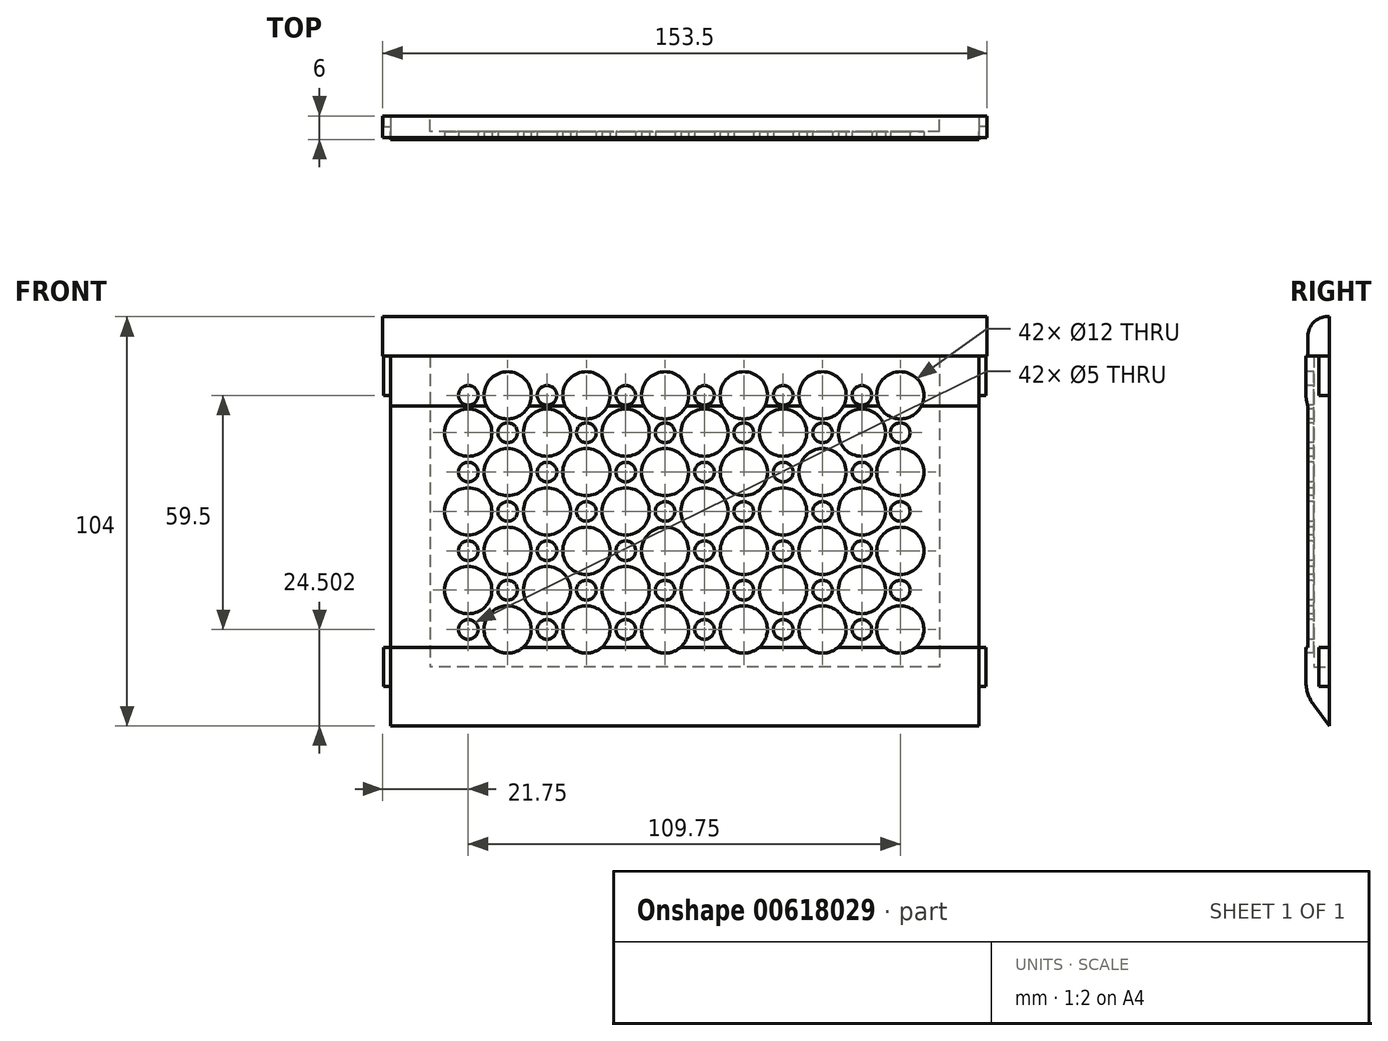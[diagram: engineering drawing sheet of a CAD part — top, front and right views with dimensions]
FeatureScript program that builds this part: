
annotation { "Feature Type Name" : "Feature", "Feature Type Description" : "" }
export const myFeature = defineFeature(function(context is Context, id is Id, definition is map)
    precondition{}
    {
        {
            var Q0;
            Q0=qCreatedBy(makeId("Right.planeOp"),FACE);
            var sketch = newSketch(context, id + "F0", { "sketchPlane" : qUnion([Q0])});
            skLineSegment(sketch, "E0", {"start": v(5.5, 58.2) * mm, "end": v(5.5, -45.8) * mm});
            skLineSegment(sketch, "E1", {"start": v(5.5, 38.2) * mm, "end": v(2.5, 38.2) * mm});
            skLineSegment(sketch, "E2", {"start": v(2.5, 38.2) * mm, "end": v(2.5, 48.2) * mm});
            skLineSegment(sketch, "E3", {"start": v(2.5, 48.2) * mm, "end": v(-0.5, 48.2) * mm});
            skLineSegment(sketch, "E4", {"start": v(-0.5, 48.2) * mm, "end": v(-0.5, 36.2) * mm});
            skLineSegment(sketch, "E5", {"start": v(-0.5, 36.2) * mm, "end": v(5.5, 28.2) * mm});
            skLineSegment(sketch, "E6", {"start": v(5.5, -45.8) * mm, "end": v(-0.5, -37.8) * mm});
            skLineSegment(sketch, "E7", {"start": v(-0.5, -37.8) * mm, "end": v(-0.5, -25.8) * mm});
            skLineSegment(sketch, "E8", {"start": v(-0.5, -25.8) * mm, "end": v(2.5, -25.8) * mm});
            skLineSegment(sketch, "E9", {"start": v(2.5, -25.8) * mm, "end": v(2.5, -35.8) * mm});
            skLineSegment(sketch, "E10", {"start": v(2.5, -35.8) * mm, "end": v(5.5, -35.8) * mm});
            skLineSegment(sketch, "E11.bottom", {"start": v(5.5, 58.2) * mm, "end": v(0, 58.2) * mm});
            skLineSegment(sketch, "E11.top", {"start": v(5.5, -45.8) * mm, "end": v(0, -45.8) * mm});
            skLineSegment(sketch, "E11.right", {"start": v(0, 58.2) * mm, "end": v(0, -45.8) * mm});
            skSolve(sketch);
        }
        {
            var Q0;
            {var subQ5=sQuery(id+"F0.wireOp",EDGE,"E1");Q0=makeQuery(id+"F0.imprint","IMPRINT",FACE,{"disambiguationData":[TD([[makeQuery(id+"F0.imprint","IMPRINT",EDGE,{"derivedFrom":subQ5}),-1.0]])]});}
            var Q1;
            {var subQ8=sQuery(id+"F0.wireOp",EDGE,"E1");Q1=makeQuery(id+"F0.imprint","IMPRINT",FACE,{"disambiguationData":[TD([[makeQuery(id+"F0.imprint","IMPRINT",EDGE,{"derivedFrom":subQ8}),1.0]])]});}
            var Q2;
            {var subQ1=sQuery(id+"F0.wireOp",EDGE,"E9");Q2=makeQuery(id+"F0.imprint","IMPRINT",FACE,{"disambiguationData":[TD([[makeQuery(id+"F0.imprint","IMPRINT",EDGE,{"derivedFrom":subQ1}),1.0]])]});}
            var Q3;
            {var subQ1=sQuery(id+"F0.wireOp",EDGE,"E9");Q3=makeQuery(id+"F0.imprint","IMPRINT",FACE,{"disambiguationData":[TD([[makeQuery(id+"F0.imprint","IMPRINT",EDGE,{"derivedFrom":subQ1}),-1.0]])]});}
            var Q4;
            {var subQ0=sQuery(id+"F0.wireOp",EDGE,"E4");Q4=makeQuery(id+"F0.imprint","IMPRINT",FACE,{"disambiguationData":[TD([[makeQuery(id+"F0.imprint","IMPRINT",EDGE,{"derivedFrom":subQ0}),1.0]])]});}
            var Q5;
            {var subQ0=sQuery(id+"F0.wireOp",EDGE,"E7");Q5=makeQuery(id+"F0.imprint","IMPRINT",FACE,{"disambiguationData":[TD([[makeQuery(id+"F0.imprint","IMPRINT",EDGE,{"derivedFrom":subQ0}),-1.0]])]});}
            extrude(context, id + "F1", {"entities" : qUnion([Q0, Q1, Q2, Q3, Q4, Q5]), "oppositeDirection" : true, "depth" : 149.5 * mm, "offsetDistance" : 25 * mm});
        }
        {
            var Q0;
            Q0=makeQuery(id+"F1.opExtrude","CAP_FACE",FACE,{"disambiguationData":[OSD([sQuery(id+"F0.wireOp",EDGE,"E3"),sQuery(id+"F0.wireOp",EDGE,"E4"),sQuery(id+"F0.wireOp",EDGE,"E5"),sQuery(id+"F0.wireOp",EDGE,"E6"),sQuery(id+"F0.wireOp",EDGE,"E7"),sQuery(id+"F0.wireOp",EDGE,"E8"),sQuery(id+"F0.wireOp",EDGE,"E11.bottom"),sQuery(id+"F0.wireOp",EDGE,"E0"),sQuery(id+"F0.wireOp",EDGE,"E11.right")])],"isStart":false});
            var sketch = newSketch(context, id + "F2", { "sketchPlane" : qUnion([Q0])});
            skLineSegment(sketch, "E12.bottom", {"start": v(-5.5, 48.2) * mm, "end": v(-2.75, 48.2) * mm});
            skLineSegment(sketch, "E12.top", {"start": v(-5.5, 38.2) * mm, "end": v(-2.75, 38.2) * mm});
            skLineSegment(sketch, "E12.left", {"start": v(-5.5, 48.2) * mm, "end": v(-5.5, 38.2) * mm});
            skLineSegment(sketch, "E12.right", {"start": v(-2.75, 48.2) * mm, "end": v(-2.75, 38.2) * mm});
            skLineSegment(sketch, "E13.bottom", {"start": v(-5.5, -25.8) * mm, "end": v(-2.75, -25.8) * mm});
            skLineSegment(sketch, "E13.top", {"start": v(-5.5, -35.8) * mm, "end": v(-2.75, -35.8) * mm});
            skLineSegment(sketch, "E13.left", {"start": v(-5.5, -25.8) * mm, "end": v(-5.5, -35.8) * mm});
            skLineSegment(sketch, "E13.right", {"start": v(-2.75, -25.8) * mm, "end": v(-2.75, -35.8) * mm});
            skSolve(sketch);
        }
        {
            var Q0;
            Q0=makeQuery(id+"F2.imprint","IMPRINT",FACE,{"disambiguationData":[TD([[makeQuery(id+"F2.imprint","IMPRINT",EDGE,{"derivedFrom":sQuery(id+"F2.wireOp",EDGE,"E12.bottom")}),-1.0]])]});
            var Q1;
            Q1=makeQuery(id+"F2.imprint","IMPRINT",FACE,{"disambiguationData":[TD([[makeQuery(id+"F2.imprint","IMPRINT",EDGE,{"derivedFrom":sQuery(id+"F2.wireOp",EDGE,"E13.bottom")}),-1.0]])]});
            extrude(context, id + "F3", {"entities" : qUnion([Q0, Q1]), "operationType" : NewBodyOperationType.ADD, "depth" : 1.75 * mm, "offsetDistance" : 25 * mm});
        }
        {
            var Q0;
            Q0=makeQuery(id+"F1.opExtrude","CAP_FACE",FACE,{"disambiguationData":[OSD([sQuery(id+"F0.wireOp",EDGE,"E3"),sQuery(id+"F0.wireOp",EDGE,"E4"),sQuery(id+"F0.wireOp",EDGE,"E5"),sQuery(id+"F0.wireOp",EDGE,"E6"),sQuery(id+"F0.wireOp",EDGE,"E7"),sQuery(id+"F0.wireOp",EDGE,"E8"),sQuery(id+"F0.wireOp",EDGE,"E11.bottom"),sQuery(id+"F0.wireOp",EDGE,"E0"),sQuery(id+"F0.wireOp",EDGE,"E11.right")])],"isStart":true});
            var sketch = newSketch(context, id + "F4", { "sketchPlane" : qUnion([Q0])});
            skLineSegment(sketch, "E14.bottom", {"start": v(5.5, 48.2) * mm, "end": v(2.75, 48.2) * mm});
            skLineSegment(sketch, "E14.top", {"start": v(5.5, 38.2) * mm, "end": v(2.75, 38.2) * mm});
            skLineSegment(sketch, "E14.left", {"start": v(5.5, 38.2) * mm, "end": v(5.5, 48.2) * mm});
            skLineSegment(sketch, "E14.right", {"start": v(2.75, 38.2) * mm, "end": v(2.75, 48.2) * mm});
            skLineSegment(sketch, "E15.bottom", {"start": v(5.5, -25.8) * mm, "end": v(2.75, -25.8) * mm});
            skLineSegment(sketch, "E15.top", {"start": v(5.5, -35.8) * mm, "end": v(2.75, -35.8) * mm});
            skLineSegment(sketch, "E15.left", {"start": v(5.5, -25.8) * mm, "end": v(5.5, -35.8) * mm});
            skLineSegment(sketch, "E15.right", {"start": v(2.75, -25.8) * mm, "end": v(2.75, -35.8) * mm});
            skSolve(sketch);
        }
        {
            var Q0;
            Q0=makeQuery(id+"F4.imprint","IMPRINT",FACE,{"disambiguationData":[TD([[makeQuery(id+"F4.imprint","IMPRINT",EDGE,{"derivedFrom":sQuery(id+"F4.wireOp",EDGE,"E15.bottom")}),1.0]])]});
            var Q1;
            Q1=makeQuery(id+"F4.imprint","IMPRINT",FACE,{"disambiguationData":[TD([[makeQuery(id+"F4.imprint","IMPRINT",EDGE,{"derivedFrom":sQuery(id+"F4.wireOp",EDGE,"E14.bottom")}),1.0]])]});
            extrude(context, id + "F5", {"entities" : qUnion([Q0, Q1]), "operationType" : NewBodyOperationType.ADD, "depth" : 1.75 * mm, "offsetDistance" : 25 * mm});
        }
        {
            var Q0;
            Q0=makeQuery(id+"F1.opExtrude","SWEPT_EDGE",EDGE,{"disambiguationData":[OSD([sQuery(id+"F0.wireOp",EDGE,"E11.bottom"),sQuery(id+"F0.wireOp",EDGE,"E11.right")])]});
            fillet(context, id + "F6", {"entities" : qUnion([Q0]), "radius" : 5 * mm, "tangentPropagation" : true, "allowEdgeOverflow" : false});
        }
        {
            var Q0;
            Q0=makeQuery(id+"F1.opExtrude","SWEPT_EDGE",EDGE,{"disambiguationData":[OSD([sQuery(id+"F0.wireOp",EDGE,"E4"),sQuery(id+"F0.wireOp",EDGE,"E5")])]});
            var Q1;
            Q1=makeQuery(id+"F1.opExtrude","SWEPT_EDGE",EDGE,{"disambiguationData":[OSD([sQuery(id+"F0.wireOp",EDGE,"E6"),sQuery(id+"F0.wireOp",EDGE,"E7")])]});
            fillet(context, id + "F7", {"entities" : qUnion([Q0, Q1]), "radius" : 10 * mm, "tangentPropagation" : true, "allowEdgeOverflow" : false});
        }
        {
            var Q0;
            Q0=makeQuery(id+"F5.boolean.opBoolean","MERGE",FACE,{"derivedFrom":[makeQuery(id+"F3.boolean.opBoolean","MERGE",FACE,{"derivedFrom":[makeQuery(id+"F1.opExtrude","SWEPT_FACE",FACE,{"disambiguationData":[OSD([sQuery(id+"F0.wireOp",EDGE,"E0")])]}),makeQuery(id+"F3.opExtrude","SWEPT_FACE",FACE,{"disambiguationData":[OSD([sQuery(id+"F2.wireOp",EDGE,"E12.left")])]}),makeQuery(id+"F3.opExtrude","SWEPT_FACE",FACE,{"disambiguationData":[OSD([sQuery(id+"F2.wireOp",EDGE,"E13.left")])]})]}),makeQuery(id+"F5.opExtrude","SWEPT_FACE",FACE,{"disambiguationData":[OSD([sQuery(id+"F4.wireOp",EDGE,"E14.left")])]}),makeQuery(id+"F5.opExtrude","SWEPT_FACE",FACE,{"disambiguationData":[OSD([sQuery(id+"F4.wireOp",EDGE,"E15.left")])]})]});
            var sketch = newSketch(context, id + "F8", { "sketchPlane" : qUnion([Q0])});
            skLineSegment(sketch, "E16.bottom", {"start": v(10, 48.2) * mm, "end": v(139.5, 48.2) * mm});
            skLineSegment(sketch, "E16.top", {"start": v(10, -30.8) * mm, "end": v(139.5, -30.8) * mm});
            skLineSegment(sketch, "E16.left", {"start": v(10, 48.2) * mm, "end": v(10, -30.8) * mm});
            skLineSegment(sketch, "E16.right", {"start": v(139.5, 48.2) * mm, "end": v(139.5, -30.8) * mm});
            skSolve(sketch);
        }
        {
            var Q0;
            Q0=makeQuery(id+"F8.imprint","IMPRINT",FACE,{"disambiguationData":[TD([[makeQuery(id+"F8.imprint","IMPRINT",EDGE,{"derivedFrom":sQuery(id+"F8.wireOp",EDGE,"E16.bottom")}),-1.0]])]});
            extrude(context, id + "F9", {"entities" : qUnion([Q0]), "operationType" : NewBodyOperationType.REMOVE, "oppositeDirection" : true, "depth" : 25 * mm, "offsetDistance" : 25 * mm});
        }
        {
            var Q0;
            Q0=makeQuery(id+"F9.boolean.opBoolean","COPY",FACE,{"derivedFrom":makeQuery(id+"F9.opExtrude","SWEPT_FACE",FACE,{"disambiguationData":[OSD([sQuery(id+"F8.wireOp",EDGE,"E16.right")])]})});
            var sketch = newSketch(context, id + "F10", { "sketchPlane" : qUnion([Q0])});
            skLineSegment(sketch, "E17", {"start": v(1.5, 48.2) * mm, "end": v(1.5, -30.8) * mm});
            skSolve(sketch);
        }
        {
            var Q0;
            {var subQ7=sQuery(id+"F10.wireOp",EDGE,"E17");Q0=makeQuery(id+"F10.imprint","IMPRINT",FACE,{"disambiguationData":[TD([[makeQuery(id+"F10.imprint","IMPRINT",EDGE,{"derivedFrom":subQ7}),-1.0]])]});}
            extrude(context, id + "F11", {"entities" : qUnion([Q0]), "operationType" : NewBodyOperationType.ADD, "depth" : 129.5 * mm, "offsetDistance" : 25 * mm});
        }
        {
            var Q0;
            Q0=makeQuery(id+"F11.opExtrude","SWEPT_FACE",FACE,{"disambiguationData":[OSD([sQuery(id+"F10.wireOp",EDGE,"E17")])]});
            var sketch = newSketch(context, id + "F12", { "sketchPlane" : qUnion([Q0])});
            skLineSegment(sketch, "E18", {"start": v(139.5, 38.2) * mm, "end": v(10, 38.2) * mm, "construction": true});
            skLineSegment(sketch, "E19", {"start": v(20, 38.2) * mm, "end": v(20, -30.8) * mm, "construction": true});
            skPoint(sketch, "E20", {"position": v(20, 28.7) * mm});
            skPoint(sketch, "E21", {"position": v(20, 18.7) * mm});
            skPoint(sketch, "E22", {"position": v(20, 8.7) * mm});
            skPoint(sketch, "E23", {"position": v(20, -1.3) * mm});
            skPoint(sketch, "E24", {"position": v(20, -11.3) * mm});
            skPoint(sketch, "E25", {"position": v(20, -21.3) * mm});
            skPoint(sketch, "E26", {"position": v(29.75, 38.2) * mm});
            skPoint(sketch, "E27", {"position": v(39.75, 38.2) * mm});
            skPoint(sketch, "E28", {"position": v(49.75, 38.2) * mm});
            skPoint(sketch, "E29", {"position": v(59.75, 38.2) * mm});
            skPoint(sketch, "E30", {"position": v(69.75, 38.2) * mm});
            skPoint(sketch, "E31", {"position": v(79.75, 38.2) * mm});
            skPoint(sketch, "E32", {"position": v(89.75, 38.2) * mm});
            skPoint(sketch, "E33", {"position": v(99.75, 38.2) * mm});
            skPoint(sketch, "E34", {"position": v(109.75, 38.2) * mm});
            skPoint(sketch, "E35", {"position": v(119.75, 38.2) * mm});
            skPoint(sketch, "E36", {"position": v(129.75, 38.2) * mm});
            skPoint(sketch, "E37", {"position": v(29.75, 28.7) * mm});
            skPoint(sketch, "E38", {"position": v(39.75, 18.7) * mm});
            skPoint(sketch, "E39", {"position": v(29.75, 18.7) * mm});
            skPoint(sketch, "E40", {"position": v(39.75, 28.7) * mm});
            skPoint(sketch, "E41", {"position": v(49.75, 28.7) * mm});
            skPoint(sketch, "E42", {"position": v(59.75, 28.7) * mm});
            skPoint(sketch, "E43", {"position": v(69.75, 28.7) * mm});
            skPoint(sketch, "E44", {"position": v(79.75, 28.7) * mm});
            skPoint(sketch, "E45", {"position": v(89.75, 28.7) * mm});
            skPoint(sketch, "E46", {"position": v(99.75, 28.7) * mm});
            skPoint(sketch, "E47", {"position": v(109.75, 28.7) * mm});
            skPoint(sketch, "E48", {"position": v(119.75, 28.7) * mm});
            skPoint(sketch, "E49", {"position": v(129.75, 28.7) * mm});
            skPoint(sketch, "E50", {"position": v(129.75, 18.7) * mm});
            skPoint(sketch, "E51", {"position": v(119.75, 18.7) * mm});
            skPoint(sketch, "E52", {"position": v(109.75, 18.7) * mm});
            skPoint(sketch, "E53", {"position": v(99.75, 18.7) * mm});
            skPoint(sketch, "E54", {"position": v(89.75, 18.7) * mm});
            skPoint(sketch, "E55", {"position": v(79.75, 18.7) * mm});
            skPoint(sketch, "E56", {"position": v(69.75, 18.7) * mm});
            skPoint(sketch, "E57", {"position": v(59.75, 18.7) * mm});
            skPoint(sketch, "E58", {"position": v(49.75, 18.7) * mm});
            skPoint(sketch, "E59", {"position": v(29.75, 8.7) * mm});
            skPoint(sketch, "E60", {"position": v(39.75, 8.7) * mm});
            skPoint(sketch, "E61", {"position": v(49.75, 8.7) * mm});
            skPoint(sketch, "E62", {"position": v(59.75, 8.7) * mm});
            skPoint(sketch, "E63", {"position": v(69.75, 8.7) * mm});
            skPoint(sketch, "E64", {"position": v(79.75, 8.7) * mm});
            skPoint(sketch, "E65", {"position": v(89.75, 8.7) * mm});
            skPoint(sketch, "E66", {"position": v(99.75, 8.7) * mm});
            skPoint(sketch, "E67", {"position": v(109.75, 8.7) * mm});
            skPoint(sketch, "E68", {"position": v(119.75, 8.7) * mm});
            skPoint(sketch, "E69", {"position": v(129.75, 8.7) * mm});
            skPoint(sketch, "E70", {"position": v(29.75, -1.3) * mm});
            skPoint(sketch, "E71", {"position": v(39.75, -1.3) * mm});
            skPoint(sketch, "E72", {"position": v(49.75, -1.3) * mm});
            skPoint(sketch, "E73", {"position": v(59.75, -1.3) * mm});
            skPoint(sketch, "E74", {"position": v(69.75, -1.3) * mm});
            skPoint(sketch, "E75", {"position": v(79.75, -1.3) * mm});
            skPoint(sketch, "E76", {"position": v(89.75, -1.3) * mm});
            skPoint(sketch, "E77", {"position": v(99.75, -1.3) * mm});
            skPoint(sketch, "E78", {"position": v(109.75, -1.3) * mm});
            skPoint(sketch, "E79", {"position": v(119.75, -1.3) * mm});
            skPoint(sketch, "E80", {"position": v(129.75, -1.3) * mm});
            skPoint(sketch, "E81", {"position": v(29.75, -11.3) * mm});
            skPoint(sketch, "E82", {"position": v(39.75, -11.3) * mm});
            skPoint(sketch, "E83", {"position": v(49.75, -11.3) * mm});
            skPoint(sketch, "E84", {"position": v(59.75, -11.3) * mm});
            skPoint(sketch, "E85", {"position": v(69.75, -11.3) * mm});
            skPoint(sketch, "E86", {"position": v(79.75, -11.3) * mm});
            skPoint(sketch, "E87", {"position": v(89.75, -11.3) * mm});
            skPoint(sketch, "E88", {"position": v(99.75, -11.3) * mm});
            skPoint(sketch, "E89", {"position": v(109.75, -11.3) * mm});
            skPoint(sketch, "E90", {"position": v(119.75, -11.3) * mm});
            skPoint(sketch, "E91", {"position": v(129.75, -11.3) * mm});
            skPoint(sketch, "E92", {"position": v(29.75, -21.3) * mm});
            skPoint(sketch, "E93", {"position": v(39.75, -21.3) * mm});
            skPoint(sketch, "E94", {"position": v(49.75, -21.3) * mm});
            skPoint(sketch, "E95", {"position": v(59.75, -21.3) * mm});
            skPoint(sketch, "E96", {"position": v(69.75, -21.3) * mm});
            skPoint(sketch, "E97", {"position": v(79.75, -21.3) * mm});
            skPoint(sketch, "E98", {"position": v(89.75, -21.3) * mm});
            skPoint(sketch, "E99", {"position": v(99.75, -21.3) * mm});
            skPoint(sketch, "E100", {"position": v(109.75, -21.3) * mm});
            skPoint(sketch, "E101", {"position": v(119.75, -21.3) * mm});
            skPoint(sketch, "E102", {"position": v(129.75, -21.3) * mm});
            skSolve(sketch);
        }
        {
            var Q0;
            Q0=sQuery(id+"F12.wireOp",VERTEX,"E25");
            var Q1;
            Q1=sQuery(id+"F12.wireOp",VERTEX,"E93");
            var Q2;
            Q2=sQuery(id+"F12.wireOp",VERTEX,"E95");
            var Q3;
            Q3=sQuery(id+"F12.wireOp",VERTEX,"E97");
            var Q4;
            Q4=sQuery(id+"F12.wireOp",VERTEX,"E99");
            var Q5;
            Q5=sQuery(id+"F12.wireOp",VERTEX,"E101");
            var Q6;
            Q6=sQuery(id+"F12.wireOp",VERTEX,"E91");
            var Q7;
            Q7=sQuery(id+"F12.wireOp",VERTEX,"E89");
            var Q8;
            Q8=sQuery(id+"F12.wireOp",VERTEX,"E87");
            var Q9;
            Q9=sQuery(id+"F12.wireOp",VERTEX,"E85");
            var Q10;
            Q10=sQuery(id+"F12.wireOp",VERTEX,"E83");
            var Q11;
            Q11=sQuery(id+"F12.wireOp",VERTEX,"E81");
            var Q12;
            Q12=sQuery(id+"F12.wireOp",VERTEX,"E23");
            var Q13;
            Q13=sQuery(id+"F12.wireOp",VERTEX,"E71");
            var Q14;
            Q14=sQuery(id+"F12.wireOp",VERTEX,"E73");
            var Q15;
            Q15=sQuery(id+"F12.wireOp",VERTEX,"E75");
            var Q16;
            Q16=sQuery(id+"F12.wireOp",VERTEX,"E77");
            var Q17;
            Q17=sQuery(id+"F12.wireOp",VERTEX,"E79");
            var Q18;
            Q18=sQuery(id+"F12.wireOp",VERTEX,"E69");
            var Q19;
            Q19=sQuery(id+"F12.wireOp",VERTEX,"E67");
            var Q20;
            Q20=sQuery(id+"F12.wireOp",VERTEX,"E65");
            var Q21;
            Q21=sQuery(id+"F12.wireOp",VERTEX,"E63");
            var Q22;
            Q22=sQuery(id+"F12.wireOp",VERTEX,"E61");
            var Q23;
            Q23=sQuery(id+"F12.wireOp",VERTEX,"E59");
            var Q24;
            Q24=sQuery(id+"F12.wireOp",VERTEX,"E21");
            var Q25;
            Q25=sQuery(id+"F12.wireOp",VERTEX,"E38");
            var Q26;
            Q26=sQuery(id+"F12.wireOp",VERTEX,"E57");
            var Q27;
            Q27=sQuery(id+"F12.wireOp",VERTEX,"E55");
            var Q28;
            Q28=sQuery(id+"F12.wireOp",VERTEX,"E53");
            var Q29;
            Q29=sQuery(id+"F12.wireOp",VERTEX,"E51");
            var Q30;
            Q30=sQuery(id+"F12.wireOp",VERTEX,"E49");
            var Q31;
            Q31=sQuery(id+"F12.wireOp",VERTEX,"E47");
            var Q32;
            Q32=sQuery(id+"F12.wireOp",VERTEX,"E45");
            var Q33;
            Q33=sQuery(id+"F12.wireOp",VERTEX,"E43");
            var Q34;
            Q34=sQuery(id+"F12.wireOp",VERTEX,"E41");
            var Q35;
            Q35=sQuery(id+"F12.wireOp",VERTEX,"E37");
            var Q36;
            Q36=sQuery(id+"F12.wireOp",VERTEX,"E19.start");
            var Q37;
            Q37=sQuery(id+"F12.wireOp",VERTEX,"E27");
            var Q38;
            Q38=sQuery(id+"F12.wireOp",VERTEX,"E29");
            var Q39;
            Q39=sQuery(id+"F12.wireOp",VERTEX,"E31");
            var Q40;
            Q40=sQuery(id+"F12.wireOp",VERTEX,"E33");
            var Q41;
            Q41=sQuery(id+"F12.wireOp",VERTEX,"E35");
            var Q42;
            Q42=makeQuery(id+"F1.opExtrude","SWEPT_BODY",BODY,{"disambiguationData":[OSD([sQuery(id+"F0.wireOp",EDGE,"E3"),sQuery(id+"F0.wireOp",EDGE,"E4"),sQuery(id+"F0.wireOp",EDGE,"E5"),sQuery(id+"F0.wireOp",EDGE,"E6"),sQuery(id+"F0.wireOp",EDGE,"E7"),sQuery(id+"F0.wireOp",EDGE,"E8"),sQuery(id+"F0.wireOp",EDGE,"E11.bottom"),sQuery(id+"F0.wireOp",EDGE,"E0"),sQuery(id+"F0.wireOp",EDGE,"E11.right")])]});
            hole(context, id + "F13", {"style" : HoleStyle.SIMPLE, "endStyle" : HoleEndStyle.BLIND, "holeDiameter" : 12 * mm, "majorDiameter" : 5 * mm, "holeDepth" : 12 * mm, "isTappedThrough" : true, "tappedDepth" : 12 * mm, "tapClearance" : 3, "locations" : qUnion([Q0, Q1, Q2, Q3, Q4, Q5, Q6, Q7, Q8, Q9, Q10, Q11, Q12, Q13, Q14, Q15, Q16, Q17, Q18, Q19, Q20, Q21, Q22, Q23, Q24, Q25, Q26, Q27, Q28, Q29, Q30, Q31, Q32, Q33, Q34, Q35, Q36, Q37, Q38, Q39, Q40, Q41]), "scope" : qUnion([Q42])});
        }
        {
            var Q0;
            Q0=sQuery(id+"F12.wireOp",VERTEX,"E26");
            var Q1;
            Q1=sQuery(id+"F12.wireOp",VERTEX,"E28");
            var Q2;
            Q2=sQuery(id+"F12.wireOp",VERTEX,"E30");
            var Q3;
            Q3=sQuery(id+"F12.wireOp",VERTEX,"E32");
            var Q4;
            Q4=sQuery(id+"F12.wireOp",VERTEX,"E34");
            var Q5;
            Q5=sQuery(id+"F12.wireOp",VERTEX,"E36");
            var Q6;
            Q6=sQuery(id+"F12.wireOp",VERTEX,"E48");
            var Q7;
            Q7=sQuery(id+"F12.wireOp",VERTEX,"E46");
            var Q8;
            Q8=sQuery(id+"F12.wireOp",VERTEX,"E44");
            var Q9;
            Q9=sQuery(id+"F12.wireOp",VERTEX,"E42");
            var Q10;
            Q10=sQuery(id+"F12.wireOp",VERTEX,"E40");
            var Q11;
            Q11=sQuery(id+"F12.wireOp",VERTEX,"E20");
            var Q12;
            Q12=sQuery(id+"F12.wireOp",VERTEX,"E39");
            var Q13;
            Q13=sQuery(id+"F12.wireOp",VERTEX,"E58");
            var Q14;
            Q14=sQuery(id+"F12.wireOp",VERTEX,"E56");
            var Q15;
            Q15=sQuery(id+"F12.wireOp",VERTEX,"E54");
            var Q16;
            Q16=sQuery(id+"F12.wireOp",VERTEX,"E52");
            var Q17;
            Q17=sQuery(id+"F12.wireOp",VERTEX,"E50");
            var Q18;
            Q18=sQuery(id+"F12.wireOp",VERTEX,"E68");
            var Q19;
            Q19=sQuery(id+"F12.wireOp",VERTEX,"E66");
            var Q20;
            Q20=sQuery(id+"F12.wireOp",VERTEX,"E64");
            var Q21;
            Q21=sQuery(id+"F12.wireOp",VERTEX,"E62");
            var Q22;
            Q22=sQuery(id+"F12.wireOp",VERTEX,"E60");
            var Q23;
            Q23=sQuery(id+"F12.wireOp",VERTEX,"E22");
            var Q24;
            Q24=sQuery(id+"F12.wireOp",VERTEX,"E70");
            var Q25;
            Q25=sQuery(id+"F12.wireOp",VERTEX,"E72");
            var Q26;
            Q26=sQuery(id+"F12.wireOp",VERTEX,"E74");
            var Q27;
            Q27=sQuery(id+"F12.wireOp",VERTEX,"E76");
            var Q28;
            Q28=sQuery(id+"F12.wireOp",VERTEX,"E78");
            var Q29;
            Q29=sQuery(id+"F12.wireOp",VERTEX,"E80");
            var Q30;
            Q30=sQuery(id+"F12.wireOp",VERTEX,"E90");
            var Q31;
            Q31=sQuery(id+"F12.wireOp",VERTEX,"E88");
            var Q32;
            Q32=sQuery(id+"F12.wireOp",VERTEX,"E86");
            var Q33;
            Q33=sQuery(id+"F12.wireOp",VERTEX,"E84");
            var Q34;
            Q34=sQuery(id+"F12.wireOp",VERTEX,"E82");
            var Q35;
            Q35=sQuery(id+"F12.wireOp",VERTEX,"E24");
            var Q36;
            Q36=sQuery(id+"F12.wireOp",VERTEX,"E92");
            var Q37;
            Q37=sQuery(id+"F12.wireOp",VERTEX,"E94");
            var Q38;
            Q38=sQuery(id+"F12.wireOp",VERTEX,"E96");
            var Q39;
            Q39=sQuery(id+"F12.wireOp",VERTEX,"E98");
            var Q40;
            Q40=sQuery(id+"F12.wireOp",VERTEX,"E100");
            var Q41;
            Q41=sQuery(id+"F12.wireOp",VERTEX,"E102");
            var Q42;
            Q42=makeQuery(id+"F1.opExtrude","SWEPT_BODY",BODY,{"disambiguationData":[OSD([sQuery(id+"F0.wireOp",EDGE,"E3"),sQuery(id+"F0.wireOp",EDGE,"E4"),sQuery(id+"F0.wireOp",EDGE,"E5"),sQuery(id+"F0.wireOp",EDGE,"E6"),sQuery(id+"F0.wireOp",EDGE,"E7"),sQuery(id+"F0.wireOp",EDGE,"E8"),sQuery(id+"F0.wireOp",EDGE,"E11.bottom"),sQuery(id+"F0.wireOp",EDGE,"E0"),sQuery(id+"F0.wireOp",EDGE,"E11.right")])]});
            hole(context, id + "F14", {"style" : HoleStyle.SIMPLE, "endStyle" : HoleEndStyle.BLIND, "holeDiameter" : 5 * mm, "majorDiameter" : 5 * mm, "holeDepth" : 12 * mm, "isTappedThrough" : true, "tappedDepth" : 12 * mm, "tapClearance" : 3, "locations" : qUnion([Q0, Q1, Q2, Q3, Q4, Q5, Q6, Q7, Q8, Q9, Q10, Q11, Q12, Q13, Q14, Q15, Q16, Q17, Q18, Q19, Q20, Q21, Q22, Q23, Q24, Q25, Q26, Q27, Q28, Q29, Q30, Q31, Q32, Q33, Q34, Q35, Q36, Q37, Q38, Q39, Q40, Q41]), "scope" : qUnion([Q42])});
        }
        {
            var Q0;
            Q0=makeQuery(id+"F1.opExtrude","CAP_FACE",FACE,{"disambiguationData":[OSD([sQuery(id+"F0.wireOp",EDGE,"E3"),sQuery(id+"F0.wireOp",EDGE,"E4"),sQuery(id+"F0.wireOp",EDGE,"E5"),sQuery(id+"F0.wireOp",EDGE,"E6"),sQuery(id+"F0.wireOp",EDGE,"E7"),sQuery(id+"F0.wireOp",EDGE,"E8"),sQuery(id+"F0.wireOp",EDGE,"E11.bottom"),sQuery(id+"F0.wireOp",EDGE,"E0"),sQuery(id+"F0.wireOp",EDGE,"E11.right")])],"isStart":false});
            var sketch = newSketch(context, id + "F15", { "sketchPlane" : qUnion([Q0])});
            skLineSegment(sketch, "E103", {"start": v(-2.75, 48.2) * mm, "end": v(0, 48.2) * mm});
            skSolve(sketch);
        }
        {
            var Q0;
            Q0=makeQuery(id+"F15.imprint","IMPRINT",FACE,{"disambiguationData":[TD([[makeQuery(id+"F15.imprint","IMPRINT",EDGE,{"derivedFrom":sQuery(id+"F15.wireOp",EDGE,"E103")}),1.0]])]});
            extrude(context, id + "F16", {"entities" : qUnion([Q0]), "operationType" : NewBodyOperationType.ADD, "depth" : 2 * mm, "offsetDistance" : 25 * mm});
        }
        {
            var Q0;
            Q0=makeQuery(id+"F1.opExtrude","CAP_FACE",FACE,{"disambiguationData":[OSD([sQuery(id+"F0.wireOp",EDGE,"E3"),sQuery(id+"F0.wireOp",EDGE,"E4"),sQuery(id+"F0.wireOp",EDGE,"E5"),sQuery(id+"F0.wireOp",EDGE,"E6"),sQuery(id+"F0.wireOp",EDGE,"E7"),sQuery(id+"F0.wireOp",EDGE,"E8"),sQuery(id+"F0.wireOp",EDGE,"E11.bottom"),sQuery(id+"F0.wireOp",EDGE,"E0"),sQuery(id+"F0.wireOp",EDGE,"E11.right")])],"isStart":true});
            var sketch = newSketch(context, id + "F17", { "sketchPlane" : qUnion([Q0])});
            skLineSegment(sketch, "E104", {"start": v(2.75, 48.2) * mm, "end": v(0, 48.2) * mm});
            skSolve(sketch);
        }
        {
            var Q0;
            Q0=makeQuery(id+"F17.imprint","IMPRINT",FACE,{"disambiguationData":[TD([[makeQuery(id+"F17.imprint","IMPRINT",EDGE,{"derivedFrom":sQuery(id+"F17.wireOp",EDGE,"E104")}),-1.0]])]});
            extrude(context, id + "F18", {"entities" : qUnion([Q0]), "operationType" : NewBodyOperationType.ADD, "depth" : 2 * mm, "offsetDistance" : 25 * mm});
        }
    });
